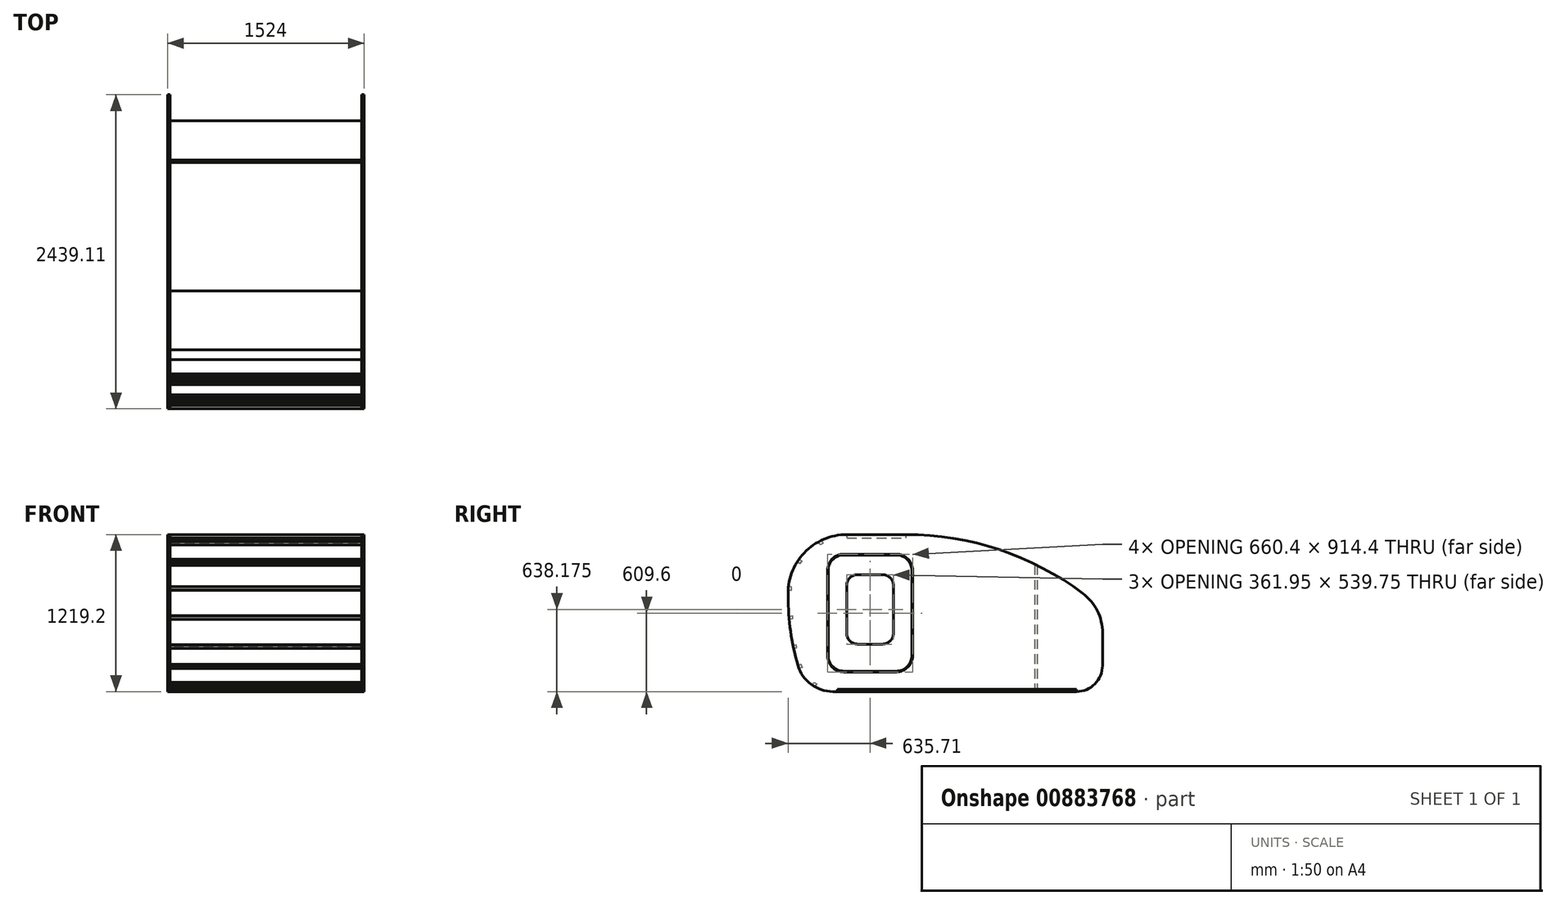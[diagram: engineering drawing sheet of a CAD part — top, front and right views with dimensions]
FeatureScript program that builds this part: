
annotation { "Feature Type Name" : "Feature", "Feature Type Description" : "" }
export const myFeature = defineFeature(function(context is Context, id is Id, definition is map)
    precondition{}
    {
        {
            var Q0;
            Q0=qCreatedBy(makeId("Right.planeOp"),FACE);
            cPlane(context, id + "F0", {"entities" : qUnion([Q0]), "cplaneType" : CPlaneType.OFFSET, "offset" : 762 * mm, "width" : 150 * mm, "height" : 150 * mm});
        }
        {
            var Q0;
            Q0=qCreatedBy(id+"F0.planeOp",FACE);
            var sketch = newSketch(context, id + "F1", { "sketchPlane" : qUnion([Q0])});
            skLineSegment(sketch, "E0.bottom", {"start": v(1219.2, -609.6) * mm, "end": v(-1219.2, -609.6) * mm, "construction": true});
            skLineSegment(sketch, "E0.top", {"start": v(1219.2, 609.6) * mm, "end": v(-1219.2, 609.6) * mm, "construction": true});
            skLineSegment(sketch, "E0.left", {"start": v(1219.2, -609.6) * mm, "end": v(1219.2, 609.6) * mm, "construction": true});
            skLineSegment(sketch, "E0.right", {"start": v(-1219.2, -609.6) * mm, "end": v(-1219.2, 609.6) * mm, "construction": true});
            skPoint(sketch, "E0.middle", {"position": v(0, 0) * mm});
            skSolve(sketch);
        }
        {
            var Q0;
            Q0=qCreatedBy(id+"F0.planeOp",FACE);
            var sketch = newSketch(context, id + "F2", { "sketchPlane" : qUnion([Q0])});
            skArc(sketch, "E1", {"start": v(1016, -609.6) * mm, "mid": v(1159.68, -550.08) * mm, "end": v(1219.2, -406.4) * mm});
            skArc(sketch, "E2", {"start": v(-1219.2, 127) * mm, "mid": v(-1200.05, -142.4) * mm, "end": v(-1143, -406.4) * mm});
            skArc(sketch, "E3", {"start": v(-762.7, 609.6) * mm, "mid": v(-1094.85, 466.58) * mm, "end": v(-1219.2, 127) * mm});
            skLineSegment(sketch, "E4", {"start": v(-762.7, 609.6) * mm, "end": v(-305.5, 609.6) * mm});
            skArc(sketch, "E5", {"start": v(-1143, -406.4) * mm, "mid": v(-1041.4, -553.16) * mm, "end": v(-872.07, -609.6) * mm});
            skArc(sketch, "E6", {"start": v(1066.69, 152.48) * mm, "mid": v(417.66, 492.32) * mm, "end": v(-305.5, 609.6) * mm});
            skArc(sketch, "E7", {"start": v(1219.2, -152.4) * mm, "mid": v(1178.95, 18.05) * mm, "end": v(1066.69, 152.48) * mm});
            skLineSegment(sketch, "E8", {"start": v(1219.2, -152.4) * mm, "end": v(1219.2, -406.4) * mm});
            skLineSegment(sketch, "E9", {"start": v(-872.07, -609.6) * mm, "end": v(1016, -609.6) * mm});
            skSolve(sketch);
        }
        {
            var Q0;
            Q0=makeQuery(id+"F2.imprint","IMPRINT",FACE,{"disambiguationData":[TD([[makeQuery(id+"F2.imprint","IMPRINT",EDGE,{"derivedFrom":sQuery(id+"F2.wireOp",EDGE,"E1")}),1.0]])]});
            extrude(context, id + "F3", {"entities" : qUnion([Q0]), "oppositeDirection" : true, "depth" : 19.05 * mm, "offsetDistance" : 25.4 * mm});
        }
        {
            var Q0;
            Q0=makeQuery(id+"F3.opExtrude","CAP_FACE",FACE,{"disambiguationData":[OSD([sQuery(id+"F2.wireOp",EDGE,"E1"),sQuery(id+"F2.wireOp",EDGE,"E2"),sQuery(id+"F2.wireOp",EDGE,"E3"),sQuery(id+"F2.wireOp",EDGE,"E4"),sQuery(id+"F2.wireOp",EDGE,"E5"),sQuery(id+"F2.wireOp",EDGE,"E6"),sQuery(id+"F2.wireOp",EDGE,"E7"),sQuery(id+"F2.wireOp",EDGE,"E8"),sQuery(id+"F2.wireOp",EDGE,"E9")])],"isStart":true});
            var sketch = newSketch(context, id + "F4", { "sketchPlane" : qUnion([Q0])});
            skLineSegment(sketch, "E10.bottom", {"start": v(-787.4, 457.2) * mm, "end": v(-381, 457.2) * mm});
            skLineSegment(sketch, "E10.top", {"start": v(-787.4, -457.2) * mm, "end": v(-381, -457.2) * mm});
            skLineSegment(sketch, "E10.left", {"start": v(-914.4, 330.2) * mm, "end": v(-914.4, -330.2) * mm});
            skLineSegment(sketch, "E10.right", {"start": v(-254, 330.2) * mm, "end": v(-254, -330.2) * mm});
            skPoint(sketch, "E11.visualSharp", {"position": v(-914.4, -457.2) * mm});
            skArc(sketch, "E11.filletArc", {"start": v(-914.4, -330.2) * mm, "mid": v(-877.2, -420) * mm, "end": v(-787.4, -457.2) * mm});
            skPoint(sketch, "E12.visualSharp", {"position": v(-914.4, 457.2) * mm});
            skArc(sketch, "E12.filletArc", {"start": v(-787.4, 457.2) * mm, "mid": v(-877.2, 420) * mm, "end": v(-914.4, 330.2) * mm});
            skPoint(sketch, "E13.visualSharp", {"position": v(-254, 457.2) * mm});
            skArc(sketch, "E13.filletArc", {"start": v(-254, 330.2) * mm, "mid": v(-291.2, 420) * mm, "end": v(-381, 457.2) * mm});
            skPoint(sketch, "E14.visualSharp", {"position": v(-254, -457.2) * mm});
            skArc(sketch, "E14.filletArc", {"start": v(-381, -457.2) * mm, "mid": v(-291.2, -420) * mm, "end": v(-254, -330.2) * mm});
            skSolve(sketch);
        }
        {
            var Q0;
            Q0 = qSketchRegion(id + "F4", true);
            extrude(context, id + "F5", {"entities" : qUnion([Q0]), "operationType" : NewBodyOperationType.REMOVE, "oppositeDirection" : true, "depth" : 25.4 * mm, "offsetDistance" : 25.4 * mm});
        }
        {
            var Q0;
            Q0=makeQuery(id+"F3.opExtrude","CAP_FACE",FACE,{"disambiguationData":[OSD([sQuery(id+"F2.wireOp",EDGE,"E1"),sQuery(id+"F2.wireOp",EDGE,"E2"),sQuery(id+"F2.wireOp",EDGE,"E3"),sQuery(id+"F2.wireOp",EDGE,"E4"),sQuery(id+"F2.wireOp",EDGE,"E5"),sQuery(id+"F2.wireOp",EDGE,"E6"),sQuery(id+"F2.wireOp",EDGE,"E7"),sQuery(id+"F2.wireOp",EDGE,"E8"),sQuery(id+"F2.wireOp",EDGE,"E9")])],"isStart":true});
            var sketch = newSketch(context, id + "F6", { "sketchPlane" : qUnion([Q0])});
            skArc(sketch, "E15.0", {"start": v(-260.35, 330.2) * mm, "mid": v(-295.69, 415.51) * mm, "end": v(-381, 450.85) * mm});
            skLineSegment(sketch, "E15.1", {"start": v(-787.4, 450.85) * mm, "end": v(-381, 450.85) * mm});
            skLineSegment(sketch, "E15.2", {"start": v(-260.35, 330.2) * mm, "end": v(-260.35, -330.2) * mm});
            skArc(sketch, "E15.3", {"start": v(-787.4, 450.85) * mm, "mid": v(-872.71, 415.51) * mm, "end": v(-908.05, 330.2) * mm});
            skArc(sketch, "E15.4", {"start": v(-381, -450.85) * mm, "mid": v(-295.69, -415.51) * mm, "end": v(-260.35, -330.2) * mm});
            skLineSegment(sketch, "E15.5", {"start": v(-787.4, -450.85) * mm, "end": v(-381, -450.85) * mm});
            skArc(sketch, "E15.6", {"start": v(-908.05, -330.2) * mm, "mid": v(-872.71, -415.51) * mm, "end": v(-787.4, -450.85) * mm});
            skLineSegment(sketch, "E15.7", {"start": v(-908.05, 330.2) * mm, "end": v(-908.05, -330.2) * mm});
            skLineSegment(sketch, "E16.bottom", {"start": v(-487.36, -241.3) * mm, "end": v(-681.04, -241.3) * mm});
            skLineSegment(sketch, "E16.top", {"start": v(-487.36, 298.45) * mm, "end": v(-681.04, 298.45) * mm});
            skLineSegment(sketch, "E16.left", {"start": v(-403.22, -157.16) * mm, "end": v(-403.23, 214.31) * mm});
            skLineSegment(sketch, "E16.right", {"start": v(-765.17, -157.16) * mm, "end": v(-765.17, 214.31) * mm});
            skLineSegment(sketch, "E17", {"start": v(-584.2, 298.45) * mm, "end": v(-584.2, 450.85) * mm, "construction": true});
            skPoint(sketch, "E18.visualSharp", {"position": v(-403.23, 298.45) * mm});
            skArc(sketch, "E18.filletArc", {"start": v(-403.23, 214.31) * mm, "mid": v(-427.87, 273.8) * mm, "end": v(-487.36, 298.45) * mm});
            skPoint(sketch, "E19.visualSharp", {"position": v(-403.23, -241.3) * mm});
            skArc(sketch, "E19.filletArc", {"start": v(-487.36, -241.3) * mm, "mid": v(-427.87, -216.66) * mm, "end": v(-403.23, -157.16) * mm});
            skPoint(sketch, "E20.visualSharp", {"position": v(-765.17, -241.3) * mm});
            skArc(sketch, "E20.filletArc", {"start": v(-765.18, -157.16) * mm, "mid": v(-740.53, -216.66) * mm, "end": v(-681.04, -241.3) * mm});
            skPoint(sketch, "E21.visualSharp", {"position": v(-765.18, 298.45) * mm});
            skArc(sketch, "E21.filletArc", {"start": v(-681.04, 298.45) * mm, "mid": v(-740.53, 273.8) * mm, "end": v(-765.17, 214.31) * mm});
            skSolve(sketch);
        }
        {
            var Q0;
            Q0=makeQuery(id+"F6.imprint","IMPRINT",FACE,{"disambiguationData":[TD([[makeQuery(id+"F6.imprint","IMPRINT",EDGE,{"derivedFrom":sQuery(id+"F6.wireOp",EDGE,"E15.0")}),1.0]])]});
            extrude(context, id + "F7", {"entities" : qUnion([Q0]), "oppositeDirection" : true, "depth" : 18.29 * mm, "offsetDistance" : 25.4 * mm});
        }
        {
            var Q0;
            Q0=makeQuery(id+"F7.opExtrude","SWEPT_BODY",BODY,{"disambiguationData":[OSD([sQuery(id+"F6.wireOp",EDGE,"E15.0"),sQuery(id+"F6.wireOp",EDGE,"E15.1"),sQuery(id+"F6.wireOp",EDGE,"E15.2"),sQuery(id+"F6.wireOp",EDGE,"E15.3"),sQuery(id+"F6.wireOp",EDGE,"E15.4"),sQuery(id+"F6.wireOp",EDGE,"E15.5"),sQuery(id+"F6.wireOp",EDGE,"E15.6"),sQuery(id+"F6.wireOp",EDGE,"E15.7"),sQuery(id+"F6.wireOp",EDGE,"E16.bottom"),sQuery(id+"F6.wireOp",EDGE,"E16.top"),sQuery(id+"F6.wireOp",EDGE,"E16.left"),sQuery(id+"F6.wireOp",EDGE,"E16.right"),sQuery(id+"F6.wireOp",EDGE,"E18.filletArc"),sQuery(id+"F6.wireOp",EDGE,"E19.filletArc"),sQuery(id+"F6.wireOp",EDGE,"E20.filletArc"),sQuery(id+"F6.wireOp",EDGE,"E21.filletArc")])]});
            var Q1;
            Q1=makeQuery(id+"F3.opExtrude","SWEPT_BODY",BODY,{"disambiguationData":[OSD([sQuery(id+"F2.wireOp",EDGE,"E1"),sQuery(id+"F2.wireOp",EDGE,"E2"),sQuery(id+"F2.wireOp",EDGE,"E3"),sQuery(id+"F2.wireOp",EDGE,"E4"),sQuery(id+"F2.wireOp",EDGE,"E5"),sQuery(id+"F2.wireOp",EDGE,"E6"),sQuery(id+"F2.wireOp",EDGE,"E7"),sQuery(id+"F2.wireOp",EDGE,"E8"),sQuery(id+"F2.wireOp",EDGE,"E9")])]});
            var Q2;
            Q2=qCreatedBy(makeId("Right.planeOp"),FACE);
            mirror(context, id + "F8", {"entities" : qUnion([Q0, Q1]), "mirrorPlane" : qUnion([Q2])});
        }
        {
            var Q0;
            Q0=qCreatedBy(makeId("Right.planeOp"),FACE);
            var sketch = newSketch(context, id + "F9", { "sketchPlane" : qUnion([Q0])});
            skLineSegment(sketch, "E22.bottom", {"start": v(-838.2, -590.55) * mm, "end": v(1016, -590.55) * mm});
            skLineSegment(sketch, "E22.top", {"start": v(-838.2, -609.6) * mm, "end": v(1016, -609.6) * mm});
            skLineSegment(sketch, "E22.left", {"start": v(-838.2, -590.55) * mm, "end": v(-838.2, -609.6) * mm});
            skLineSegment(sketch, "E22.right", {"start": v(1016, -590.55) * mm, "end": v(1016, -609.6) * mm});
            skSolve(sketch);
        }
        {
            var Q0;
            Q0 = qSketchRegion(id + "F9", true);
            var Q1;
            Q1=makeQuery(id+"F3.opExtrude","CAP_FACE",FACE,{"disambiguationData":[OSD([sQuery(id+"F2.wireOp",EDGE,"E1"),sQuery(id+"F2.wireOp",EDGE,"E2"),sQuery(id+"F2.wireOp",EDGE,"E3"),sQuery(id+"F2.wireOp",EDGE,"E4"),sQuery(id+"F2.wireOp",EDGE,"E5"),sQuery(id+"F2.wireOp",EDGE,"E6"),sQuery(id+"F2.wireOp",EDGE,"E7"),sQuery(id+"F2.wireOp",EDGE,"E8"),sQuery(id+"F2.wireOp",EDGE,"E9")])],"isStart":true});
            var Q2;
            Q2=makeQuery(id+"F8.opPattern","COPY",FACE,{"derivedFrom":makeQuery(id+"F3.opExtrude","CAP_FACE",FACE,{"disambiguationData":[OSD([sQuery(id+"F2.wireOp",EDGE,"E1"),sQuery(id+"F2.wireOp",EDGE,"E2"),sQuery(id+"F2.wireOp",EDGE,"E3"),sQuery(id+"F2.wireOp",EDGE,"E4"),sQuery(id+"F2.wireOp",EDGE,"E5"),sQuery(id+"F2.wireOp",EDGE,"E6"),sQuery(id+"F2.wireOp",EDGE,"E7"),sQuery(id+"F2.wireOp",EDGE,"E8"),sQuery(id+"F2.wireOp",EDGE,"E9")])],"isStart":true}),"instanceName":"1"});
            extrude(context, id + "F10", {"entities" : qUnion([Q0]), "endBound" : BoundingType.UP_TO_SURFACE, "depth" : 25.4 * mm, "endBoundEntityFace" : qUnion([Q1]), "offsetDistance" : 25.4 * mm, "hasSecondDirection" : true, "secondDirectionBound" : SecondDirectionBoundingType.UP_TO_SURFACE, "secondDirectionOppositeDirection" : true, "secondDirectionDepth" : 997.98 * mm, "secondDirectionBoundEntityFace" : qUnion([Q2])});
        }
        {
            var Q0;
            Q0=makeQuery(id+"F3.opExtrude","CAP_FACE",FACE,{"disambiguationData":[OSD([sQuery(id+"F2.wireOp",EDGE,"E1"),sQuery(id+"F2.wireOp",EDGE,"E2"),sQuery(id+"F2.wireOp",EDGE,"E3"),sQuery(id+"F2.wireOp",EDGE,"E4"),sQuery(id+"F2.wireOp",EDGE,"E5"),sQuery(id+"F2.wireOp",EDGE,"E6"),sQuery(id+"F2.wireOp",EDGE,"E7"),sQuery(id+"F2.wireOp",EDGE,"E8"),sQuery(id+"F2.wireOp",EDGE,"E9")])],"isStart":false});
            var sketch = newSketch(context, id + "F11", { "sketchPlane" : qUnion([Q0])});
            skLineSegment(sketch, "E23.bottom", {"start": v(762.7, 584.2) * mm, "end": v(305.5, 584.2) * mm});
            skLineSegment(sketch, "E23.top", {"start": v(762.7, 609.6) * mm, "end": v(305.5, 609.6) * mm});
            skLineSegment(sketch, "E23.left", {"start": v(762.7, 584.2) * mm, "end": v(762.7, 609.6) * mm});
            skLineSegment(sketch, "E23.right", {"start": v(305.5, 584.2) * mm, "end": v(305.5, 609.6) * mm});
            skSolve(sketch);
        }
        {
            var Q0;
            Q0 = qSketchRegion(id + "F11", true);
            var Q1;
            Q1=makeQuery(id+"F8.opPattern","COPY",FACE,{"derivedFrom":makeQuery(id+"F3.opExtrude","CAP_FACE",FACE,{"disambiguationData":[OSD([sQuery(id+"F2.wireOp",EDGE,"E1"),sQuery(id+"F2.wireOp",EDGE,"E2"),sQuery(id+"F2.wireOp",EDGE,"E3"),sQuery(id+"F2.wireOp",EDGE,"E4"),sQuery(id+"F2.wireOp",EDGE,"E5"),sQuery(id+"F2.wireOp",EDGE,"E6"),sQuery(id+"F2.wireOp",EDGE,"E7"),sQuery(id+"F2.wireOp",EDGE,"E8"),sQuery(id+"F2.wireOp",EDGE,"E9")])],"isStart":false}),"instanceName":"1"});
            extrude(context, id + "F12", {"entities" : qUnion([Q0]), "endBound" : BoundingType.UP_TO_SURFACE, "depth" : 922.04 * mm, "endBoundEntityFace" : qUnion([Q1]), "offsetDistance" : 25.4 * mm});
        }
        {
            var Q0;
            Q0=makeQuery(id+"F3.opExtrude","CAP_FACE",FACE,{"disambiguationData":[OSD([sQuery(id+"F2.wireOp",EDGE,"E1"),sQuery(id+"F2.wireOp",EDGE,"E2"),sQuery(id+"F2.wireOp",EDGE,"E3"),sQuery(id+"F2.wireOp",EDGE,"E4"),sQuery(id+"F2.wireOp",EDGE,"E5"),sQuery(id+"F2.wireOp",EDGE,"E6"),sQuery(id+"F2.wireOp",EDGE,"E7"),sQuery(id+"F2.wireOp",EDGE,"E8"),sQuery(id+"F2.wireOp",EDGE,"E9")])],"isStart":false});
            var sketch = newSketch(context, id + "F13", { "sketchPlane" : qUnion([Q0])});
            skLineSegment(sketch, "E24", {"start": v(983.4, 552.8) * mm, "end": v(960.83, 564.44) * mm});
            skLineSegment(sketch, "E25", {"start": v(960.83, 564.44) * mm, "end": v(949.19, 541.87) * mm});
            skLineSegment(sketch, "E26", {"start": v(949.19, 541.87) * mm, "end": v(971.76, 530.23) * mm});
            skLineSegment(sketch, "E27", {"start": v(971.76, 530.23) * mm, "end": v(983.4, 552.8) * mm});
            skSolve(sketch);
        }
        {
            var Q0;
            Q0 = qSketchRegion(id + "F13", true);
            var Q1;
            Q1=makeQuery(id+"F8.opPattern","COPY",FACE,{"derivedFrom":makeQuery(id+"F3.opExtrude","CAP_FACE",FACE,{"disambiguationData":[OSD([sQuery(id+"F2.wireOp",EDGE,"E1"),sQuery(id+"F2.wireOp",EDGE,"E2"),sQuery(id+"F2.wireOp",EDGE,"E3"),sQuery(id+"F2.wireOp",EDGE,"E4"),sQuery(id+"F2.wireOp",EDGE,"E5"),sQuery(id+"F2.wireOp",EDGE,"E6"),sQuery(id+"F2.wireOp",EDGE,"E7"),sQuery(id+"F2.wireOp",EDGE,"E8"),sQuery(id+"F2.wireOp",EDGE,"E9")])],"isStart":false}),"instanceName":"1"});
            extrude(context, id + "F14", {"entities" : qUnion([Q0]), "endBound" : BoundingType.UP_TO_SURFACE, "depth" : 25.4 * mm, "endBoundEntityFace" : qUnion([Q1]), "offsetDistance" : 25.4 * mm});
        }
        {
            var Q0;
            Q0=makeQuery(id+"F3.opExtrude","CAP_FACE",FACE,{"disambiguationData":[OSD([sQuery(id+"F2.wireOp",EDGE,"E1"),sQuery(id+"F2.wireOp",EDGE,"E2"),sQuery(id+"F2.wireOp",EDGE,"E3"),sQuery(id+"F2.wireOp",EDGE,"E4"),sQuery(id+"F2.wireOp",EDGE,"E5"),sQuery(id+"F2.wireOp",EDGE,"E6"),sQuery(id+"F2.wireOp",EDGE,"E7"),sQuery(id+"F2.wireOp",EDGE,"E8"),sQuery(id+"F2.wireOp",EDGE,"E9")])],"isStart":false});
            var sketch = newSketch(context, id + "F15", { "sketchPlane" : qUnion([Q0])});
            skLineSegment(sketch, "E28", {"start": v(1135.11, 417.63) * mm, "end": v(1114.02, 403.47) * mm});
            skLineSegment(sketch, "E29", {"start": v(1114.02, 403.47) * mm, "end": v(1128.18, 382.38) * mm});
            skLineSegment(sketch, "E30", {"start": v(1128.18, 382.38) * mm, "end": v(1149.27, 396.53) * mm});
            skLineSegment(sketch, "E31", {"start": v(1149.27, 396.53) * mm, "end": v(1135.11, 417.63) * mm});
            skSolve(sketch);
        }
        {
            var Q0;
            Q0 = qSketchRegion(id + "F15", true);
            var Q1;
            Q1=makeQuery(id+"F8.opPattern","COPY",FACE,{"derivedFrom":makeQuery(id+"F3.opExtrude","CAP_FACE",FACE,{"disambiguationData":[OSD([sQuery(id+"F2.wireOp",EDGE,"E1"),sQuery(id+"F2.wireOp",EDGE,"E2"),sQuery(id+"F2.wireOp",EDGE,"E3"),sQuery(id+"F2.wireOp",EDGE,"E4"),sQuery(id+"F2.wireOp",EDGE,"E5"),sQuery(id+"F2.wireOp",EDGE,"E6"),sQuery(id+"F2.wireOp",EDGE,"E7"),sQuery(id+"F2.wireOp",EDGE,"E8"),sQuery(id+"F2.wireOp",EDGE,"E9")])],"isStart":false}),"instanceName":"1"});
            extrude(context, id + "F16", {"entities" : qUnion([Q0]), "endBound" : BoundingType.UP_TO_SURFACE, "depth" : 25.4 * mm, "endBoundEntityFace" : qUnion([Q1]), "offsetDistance" : 25.4 * mm});
        }
        {
            var Q0;
            Q0=makeQuery(id+"F8.opPattern","COPY",FACE,{"derivedFrom":makeQuery(id+"F3.opExtrude","CAP_FACE",FACE,{"disambiguationData":[OSD([sQuery(id+"F2.wireOp",EDGE,"E1"),sQuery(id+"F2.wireOp",EDGE,"E2"),sQuery(id+"F2.wireOp",EDGE,"E3"),sQuery(id+"F2.wireOp",EDGE,"E4"),sQuery(id+"F2.wireOp",EDGE,"E5"),sQuery(id+"F2.wireOp",EDGE,"E6"),sQuery(id+"F2.wireOp",EDGE,"E7"),sQuery(id+"F2.wireOp",EDGE,"E8"),sQuery(id+"F2.wireOp",EDGE,"E9")])],"isStart":false}),"instanceName":"1"});
            var sketch = newSketch(context, id + "F17", { "sketchPlane" : qUnion([Q0])});
            skLineSegment(sketch, "E32", {"start": v(-1219.1, 179.61) * mm, "end": v(-1193.8, 177.4) * mm});
            skLineSegment(sketch, "E33", {"start": v(-1193.8, 177.4) * mm, "end": v(-1191.58, 202.7) * mm});
            skLineSegment(sketch, "E34", {"start": v(-1191.58, 202.7) * mm, "end": v(-1216.88, 204.91) * mm});
            skLineSegment(sketch, "E35", {"start": v(-1216.88, 204.91) * mm, "end": v(-1219.1, 179.61) * mm});
            skSolve(sketch);
        }
        {
            var Q0;
            Q0 = qSketchRegion(id + "F17", true);
            var Q1;
            Q1=makeQuery(id+"F3.opExtrude","CAP_FACE",FACE,{"disambiguationData":[OSD([sQuery(id+"F2.wireOp",EDGE,"E1"),sQuery(id+"F2.wireOp",EDGE,"E2"),sQuery(id+"F2.wireOp",EDGE,"E3"),sQuery(id+"F2.wireOp",EDGE,"E4"),sQuery(id+"F2.wireOp",EDGE,"E5"),sQuery(id+"F2.wireOp",EDGE,"E6"),sQuery(id+"F2.wireOp",EDGE,"E7"),sQuery(id+"F2.wireOp",EDGE,"E8"),sQuery(id+"F2.wireOp",EDGE,"E9")])],"isStart":false});
            extrude(context, id + "F18", {"entities" : qUnion([Q0]), "endBound" : BoundingType.UP_TO_SURFACE, "depth" : 25.4 * mm, "endBoundEntityFace" : qUnion([Q1]), "offsetDistance" : 25.4 * mm});
        }
        {
            var Q0;
            Q0=makeQuery(id+"F3.opExtrude","CAP_FACE",FACE,{"disambiguationData":[OSD([sQuery(id+"F2.wireOp",EDGE,"E1"),sQuery(id+"F2.wireOp",EDGE,"E2"),sQuery(id+"F2.wireOp",EDGE,"E3"),sQuery(id+"F2.wireOp",EDGE,"E4"),sQuery(id+"F2.wireOp",EDGE,"E5"),sQuery(id+"F2.wireOp",EDGE,"E6"),sQuery(id+"F2.wireOp",EDGE,"E7"),sQuery(id+"F2.wireOp",EDGE,"E8"),sQuery(id+"F2.wireOp",EDGE,"E9")])],"isStart":false});
            var sketch = newSketch(context, id + "F19", { "sketchPlane" : qUnion([Q0])});
            skSolve(sketch);
        }
        {
            var Q0;
            {var subQ8=sQuery(id+"F2.wireOp",EDGE,"E1");Q0=makeQuery(id+"F19.imprint","IMPRINT",FACE,{"disambiguationData":[TD([[makeQuery(id+"F19.imprint","IMPRINT",EDGE,{"derivedFrom":makeQuery(id+"F3.opExtrude","CAP_EDGE",EDGE,{"disambiguationData":[OSD([subQ8])],"isStart":false})}),-1.0]])]});}
            var sketch = newSketch(context, id + "F20", { "sketchPlane" : qUnion([Q0])});
            skLineSegment(sketch, "E36", {"start": v(1187.94, -21.33) * mm, "end": v(1185.76, -46.64) * mm});
            skLineSegment(sketch, "E37", {"start": v(1185.76, -46.64) * mm, "end": v(1211.07, -48.81) * mm});
            skLineSegment(sketch, "E38", {"start": v(1211.07, -48.81) * mm, "end": v(1213.25, -23.5) * mm});
            skLineSegment(sketch, "E39", {"start": v(1213.25, -23.5) * mm, "end": v(1187.94, -21.33) * mm});
            skSolve(sketch);
        }
        {
            var Q0;
            Q0 = qSketchRegion(id + "F20", true);
            var Q1;
            Q1=makeQuery(id+"F8.opPattern","COPY",FACE,{"derivedFrom":makeQuery(id+"F3.opExtrude","CAP_FACE",FACE,{"disambiguationData":[OSD([sQuery(id+"F2.wireOp",EDGE,"E1"),sQuery(id+"F2.wireOp",EDGE,"E2"),sQuery(id+"F2.wireOp",EDGE,"E3"),sQuery(id+"F2.wireOp",EDGE,"E4"),sQuery(id+"F2.wireOp",EDGE,"E5"),sQuery(id+"F2.wireOp",EDGE,"E6"),sQuery(id+"F2.wireOp",EDGE,"E7"),sQuery(id+"F2.wireOp",EDGE,"E8"),sQuery(id+"F2.wireOp",EDGE,"E9")])],"isStart":false}),"instanceName":"1"});
            extrude(context, id + "F21", {"entities" : qUnion([Q0]), "endBound" : BoundingType.UP_TO_SURFACE, "depth" : 25.4 * mm, "endBoundEntityFace" : qUnion([Q1]), "offsetDistance" : 25.4 * mm});
        }
        {
            var Q0;
            Q0=makeQuery(id+"F8.opPattern","COPY",FACE,{"derivedFrom":makeQuery(id+"F3.opExtrude","CAP_FACE",FACE,{"disambiguationData":[OSD([sQuery(id+"F2.wireOp",EDGE,"E1"),sQuery(id+"F2.wireOp",EDGE,"E2"),sQuery(id+"F2.wireOp",EDGE,"E3"),sQuery(id+"F2.wireOp",EDGE,"E4"),sQuery(id+"F2.wireOp",EDGE,"E5"),sQuery(id+"F2.wireOp",EDGE,"E6"),sQuery(id+"F2.wireOp",EDGE,"E7"),sQuery(id+"F2.wireOp",EDGE,"E8"),sQuery(id+"F2.wireOp",EDGE,"E9")])],"isStart":false}),"instanceName":"1"});
            var sketch = newSketch(context, id + "F22", { "sketchPlane" : qUnion([Q0])});
            skLineSegment(sketch, "E40", {"start": v(-1181.55, -249.86) * mm, "end": v(-1176.36, -274.72) * mm});
            skLineSegment(sketch, "E41", {"start": v(-1176.36, -274.72) * mm, "end": v(-1151.5, -269.53) * mm});
            skLineSegment(sketch, "E42", {"start": v(-1151.5, -269.53) * mm, "end": v(-1156.69, -244.67) * mm});
            skLineSegment(sketch, "E43", {"start": v(-1181.55, -249.86) * mm, "end": v(-1156.69, -244.67) * mm});
            skSolve(sketch);
        }
        {
            var Q0;
            Q0 = qSketchRegion(id + "F22", true);
            var Q1;
            Q1=makeQuery(id+"F3.opExtrude","CAP_FACE",FACE,{"disambiguationData":[OSD([sQuery(id+"F2.wireOp",EDGE,"E1"),sQuery(id+"F2.wireOp",EDGE,"E2"),sQuery(id+"F2.wireOp",EDGE,"E3"),sQuery(id+"F2.wireOp",EDGE,"E4"),sQuery(id+"F2.wireOp",EDGE,"E5"),sQuery(id+"F2.wireOp",EDGE,"E6"),sQuery(id+"F2.wireOp",EDGE,"E7"),sQuery(id+"F2.wireOp",EDGE,"E8"),sQuery(id+"F2.wireOp",EDGE,"E9")])],"isStart":false});
            var Q2;
            Q2=makeQuery(id+"F3.opExtrude","SWEPT_BODY",BODY,{"disambiguationData":[OSD([sQuery(id+"F2.wireOp",EDGE,"E1"),sQuery(id+"F2.wireOp",EDGE,"E2"),sQuery(id+"F2.wireOp",EDGE,"E3"),sQuery(id+"F2.wireOp",EDGE,"E4"),sQuery(id+"F2.wireOp",EDGE,"E5"),sQuery(id+"F2.wireOp",EDGE,"E6"),sQuery(id+"F2.wireOp",EDGE,"E7"),sQuery(id+"F2.wireOp",EDGE,"E8"),sQuery(id+"F2.wireOp",EDGE,"E9")])]});
            extrude(context, id + "F23", {"entities" : qUnion([Q0]), "endBound" : BoundingType.UP_TO_SURFACE, "depth" : 25.4 * mm, "endBoundEntityFace" : qUnion([Q1]), "endBoundEntityBody" : qUnion([Q2]), "offsetDistance" : 25.4 * mm});
        }
        {
            var Q0;
            {var subQ8=sQuery(id+"F2.wireOp",EDGE,"E1");Q0=makeQuery(id+"F19.imprint","IMPRINT",FACE,{"disambiguationData":[TD([[makeQuery(id+"F19.imprint","IMPRINT",EDGE,{"derivedFrom":makeQuery(id+"F3.opExtrude","CAP_EDGE",EDGE,{"disambiguationData":[OSD([subQ8])],"isStart":false})}),-1.0]])]});}
            var sketch = newSketch(context, id + "F24", { "sketchPlane" : qUnion([Q0])});
            skLineSegment(sketch, "E44.bottom", {"start": v(1118.96, -398.2) * mm, "end": v(1143, -406.4) * mm});
            skLineSegment(sketch, "E44.top", {"start": v(1110.76, -422.24) * mm, "end": v(1134.8, -430.44) * mm});
            skLineSegment(sketch, "E44.left", {"start": v(1118.96, -398.2) * mm, "end": v(1110.76, -422.24) * mm});
            skLineSegment(sketch, "E44.right", {"start": v(1143, -406.4) * mm, "end": v(1134.8, -430.44) * mm});
            skSolve(sketch);
        }
        {
            var Q0;
            Q0 = qSketchRegion(id + "F24", true);
            var Q1;
            Q1=makeQuery(id+"F8.opPattern","COPY",FACE,{"derivedFrom":makeQuery(id+"F3.opExtrude","CAP_FACE",FACE,{"disambiguationData":[OSD([sQuery(id+"F2.wireOp",EDGE,"E1"),sQuery(id+"F2.wireOp",EDGE,"E2"),sQuery(id+"F2.wireOp",EDGE,"E3"),sQuery(id+"F2.wireOp",EDGE,"E4"),sQuery(id+"F2.wireOp",EDGE,"E5"),sQuery(id+"F2.wireOp",EDGE,"E6"),sQuery(id+"F2.wireOp",EDGE,"E7"),sQuery(id+"F2.wireOp",EDGE,"E8"),sQuery(id+"F2.wireOp",EDGE,"E9")])],"isStart":false}),"instanceName":"1"});
            extrude(context, id + "F25", {"entities" : qUnion([Q0]), "endBound" : BoundingType.UP_TO_SURFACE, "depth" : 25.4 * mm, "endBoundEntityFace" : qUnion([Q1]), "offsetDistance" : 25.4 * mm});
        }
        {
            var Q0;
            Q0=makeQuery(id+"F8.opPattern","COPY",FACE,{"derivedFrom":makeQuery(id+"F3.opExtrude","CAP_FACE",FACE,{"disambiguationData":[OSD([sQuery(id+"F2.wireOp",EDGE,"E1"),sQuery(id+"F2.wireOp",EDGE,"E2"),sQuery(id+"F2.wireOp",EDGE,"E3"),sQuery(id+"F2.wireOp",EDGE,"E4"),sQuery(id+"F2.wireOp",EDGE,"E5"),sQuery(id+"F2.wireOp",EDGE,"E6"),sQuery(id+"F2.wireOp",EDGE,"E7"),sQuery(id+"F2.wireOp",EDGE,"E8"),sQuery(id+"F2.wireOp",EDGE,"E9")])],"isStart":false}),"instanceName":"1"});
            var sketch = newSketch(context, id + "F26", { "sketchPlane" : qUnion([Q0])});
            skLineSegment(sketch, "E45.bottom", {"start": v(-1032.19, -559.78) * mm, "end": v(-1018.73, -538.24) * mm});
            skLineSegment(sketch, "E45.top", {"start": v(-1010.64, -573.24) * mm, "end": v(-997.19, -551.7) * mm});
            skLineSegment(sketch, "E45.left", {"start": v(-1032.19, -559.78) * mm, "end": v(-1010.64, -573.24) * mm});
            skLineSegment(sketch, "E45.right", {"start": v(-1018.73, -538.24) * mm, "end": v(-997.19, -551.7) * mm});
            skSolve(sketch);
        }
        {
            var Q0;
            Q0 = qSketchRegion(id + "F26", true);
            var Q1;
            Q1=makeQuery(id+"F3.opExtrude","CAP_FACE",FACE,{"disambiguationData":[OSD([sQuery(id+"F2.wireOp",EDGE,"E1"),sQuery(id+"F2.wireOp",EDGE,"E2"),sQuery(id+"F2.wireOp",EDGE,"E3"),sQuery(id+"F2.wireOp",EDGE,"E4"),sQuery(id+"F2.wireOp",EDGE,"E5"),sQuery(id+"F2.wireOp",EDGE,"E6"),sQuery(id+"F2.wireOp",EDGE,"E7"),sQuery(id+"F2.wireOp",EDGE,"E8"),sQuery(id+"F2.wireOp",EDGE,"E9")])],"isStart":false});
            extrude(context, id + "F27", {"entities" : qUnion([Q0]), "endBound" : BoundingType.UP_TO_SURFACE, "depth" : 25.4 * mm, "endBoundEntityFace" : qUnion([Q1]), "offsetDistance" : 25.4 * mm});
        }
        {
            var Q0;
            {var subQ8=sQuery(id+"F2.wireOp",EDGE,"E1");Q0=makeQuery(id+"F19.imprint","IMPRINT",FACE,{"disambiguationData":[TD([[makeQuery(id+"F19.imprint","IMPRINT",EDGE,{"derivedFrom":makeQuery(id+"F3.opExtrude","CAP_EDGE",EDGE,{"disambiguationData":[OSD([subQ8])],"isStart":false})}),-1.0]])]});}
            var sketch = newSketch(context, id + "F28", { "sketchPlane" : qUnion([Q0])});
            skLineSegment(sketch, "E46.bottom", {"start": v(-711.2, 371.3) * mm, "end": v(-692.15, 371.3) * mm});
            skLineSegment(sketch, "E46.top", {"start": v(-711.2, -590.55) * mm, "end": v(-692.15, -590.55) * mm});
            skLineSegment(sketch, "E46.left", {"start": v(-711.2, 371.3) * mm, "end": v(-711.2, -590.55) * mm});
            skLineSegment(sketch, "E46.right", {"start": v(-692.15, 371.3) * mm, "end": v(-692.15, -590.55) * mm});
            skSolve(sketch);
        }
        {
            var Q0;
            Q0 = qSketchRegion(id + "F28", true);
            var Q1;
            Q1=makeQuery(id+"F8.opPattern","COPY",FACE,{"derivedFrom":makeQuery(id+"F3.opExtrude","CAP_FACE",FACE,{"disambiguationData":[OSD([sQuery(id+"F2.wireOp",EDGE,"E1"),sQuery(id+"F2.wireOp",EDGE,"E2"),sQuery(id+"F2.wireOp",EDGE,"E3"),sQuery(id+"F2.wireOp",EDGE,"E4"),sQuery(id+"F2.wireOp",EDGE,"E5"),sQuery(id+"F2.wireOp",EDGE,"E6"),sQuery(id+"F2.wireOp",EDGE,"E7"),sQuery(id+"F2.wireOp",EDGE,"E8"),sQuery(id+"F2.wireOp",EDGE,"E9")])],"isStart":false}),"instanceName":"1"});
            extrude(context, id + "F29", {"entities" : qUnion([Q0]), "endBound" : BoundingType.UP_TO_SURFACE, "depth" : 25.4 * mm, "endBoundEntityFace" : qUnion([Q1]), "offsetDistance" : 25.4 * mm});
        }
    });
